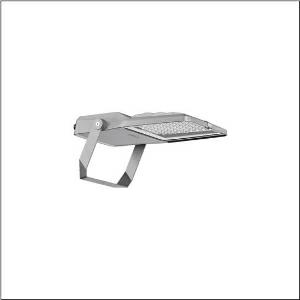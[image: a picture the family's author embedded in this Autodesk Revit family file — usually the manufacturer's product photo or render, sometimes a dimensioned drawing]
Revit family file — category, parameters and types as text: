
# Revit family: floodlight_fl_21_iq_mini___pl33t_5xa7772b4f1a_67af
name_source: partatom
category: Lighting Fixtures
units: mm (PartAtom-declared; Revit-internal decimal feet)

## family parameters
Cut with Voids When Loaded = No
Host = Face
Light Source = No
Part Type = Normal
Room Calculation Point = No
Round Connector Dimension = Use Diameter
Shared = No

## types (1)
- --- (1 x LED, 6420 lm, 45.5 W, 4000K)
    Apparent Load = 46 VA
    CIE Flux Codes = 26 75 99 100 100
    Color Rendering = 70
    Color Temperature = 4000K
    Default Elevation = 1800 mm
    Description = Floodlight FL 21 iQ mini, floodlight, primary light control with lens, of PMMA, primary optical cover: protective disc, of toughened safety glass, transparent, light distribution: PL33T, light emission: direct distribution, installation type: surface-mounted, LED, High Power LED, rated luminous flux: 6.420lm, luminous efficacy: 141lm/W, light colour: 740, colour temperature: 4000K, control gear: iQ Street-Remote/DALI, control: Street-Remote, Auto-Match, Temp-Guard, Night-Set, Smart-Wire, Desk-Remote (wireless, voltage-free reading and setting of iQ features in the workshop via application-optimized NFC function/RFID function), optimised constant luminous flux control (CLO 2.0), with terminal, 6-pole, mains connection: 220..240V, AC, 50/60Hz, start of lifetime: 46W, end of service life: 48W, reduction: 22W, luminaire housing, of diecast aluminium, powder-coated, Siteco® metallic grey (DB 702S), corrosivity category C5 mid according to DIN EN ISO 12944, suitable for swimming pools, chlorine-resistant, sealing non-destructively replaceable, mounting bracket, of steel, galvanised, powder-coated, Siteco® metallic grey (DB 702S), protection rating (complete): IP66, insulation class (complete): insulation class II (safety insulation), certification: CE, ENEC, VDE, protection symbol: D, impact resistance: IK08, permissible operating ambient temperature: -40..+40°C, permissible operating ambient temperature for outdoor applications: -40..+50°C, standard: DIN EN 12944, LABS conformity tested according to VDMA 24364:2018-05, packaging unit: 1 piece

Light Distribution: PL33T
    Height = 70 mm
    Lamp = 1 x LED
    Lamp Light Flux = 6420 lm
    Lamp Power = 45.5 W
    Lamp count = 1
    Length = 485 mm
    Luminous efficacy = 141 lm/W
    Manufacturer = Siteco
    ModVariant = No
    Model = 5XA7772B4F1A
    Number of Poles = 1
    OnlyDefault = Yes
    Power Factor = 1
    Product Name = Floodlight FL 21 iQ mini | PL33T
    Product group = floodlight | pylon annexe
    ProductGroupID = 6200
    Protection Class = Protection class II
    Protection Degree = IP 66
    RLX_Detail_Level = 1
    RLX_Emergency_Light_Flux = 0 lm
    RLX_Emergency_Type = 0
    RLX_Emergency_Type_DB = No
    RlxData = <blob elided: 96089 chars, md5=271a7a93>
    Socket = socket
    Standby Power = 0 W
    System Light Flux = 6420 lm
    System Power = 46 W
    Type Comments = factory setting: luminous flux: 100 % | dim-lin: 254 | 463 mA
    Type Image = l_1006845.jpg
    URL = http://relux.com
    VarID = @adj_149960
    Voltage = 0 V
    Weight = 0.00 kg
    Width = 337 mm

## geometry (parser evidence)
native form markers: Blend x4, Sweep x11
no freeform markers — native parametric forms only
